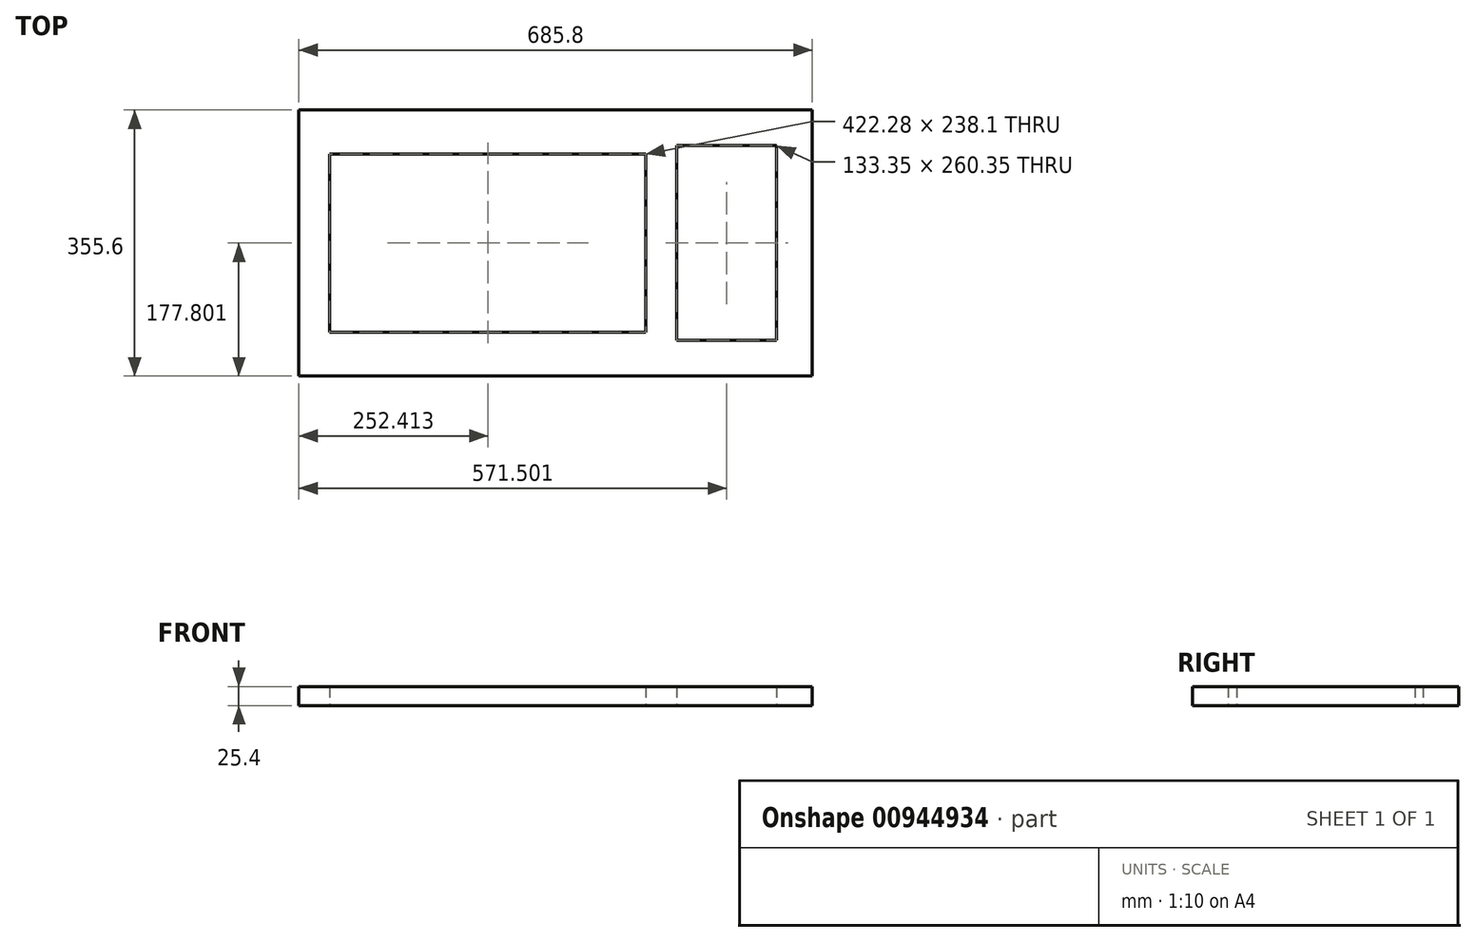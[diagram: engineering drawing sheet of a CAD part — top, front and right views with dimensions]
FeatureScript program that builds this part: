
annotation { "Feature Type Name" : "Feature", "Feature Type Description" : "" }
export const myFeature = defineFeature(function(context is Context, id is Id, definition is map)
    precondition{}
    {
        {
            var Q0;
            Q0=qCreatedBy(makeId("Top.planeOp"),FACE);
            var sketch = newSketch(context, id + "F0", { "sketchPlane" : qUnion([Q0])});
            skLineSegment(sketch, "E0.bottom", {"start": v(-348.34, 190.06) * mm, "end": v(337.46, 190.06) * mm});
            skLineSegment(sketch, "E0.top", {"start": v(-348.34, -165.54) * mm, "end": v(337.46, -165.54) * mm});
            skLineSegment(sketch, "E0.left", {"start": v(-348.34, 190.06) * mm, "end": v(-348.34, -165.54) * mm});
            skLineSegment(sketch, "E0.right", {"start": v(337.46, 190.06) * mm, "end": v(337.46, -165.54) * mm});
            skLineSegment(sketch, "E1.bottom", {"start": v(156.49, 142.44) * mm, "end": v(289.84, 142.44) * mm});
            skLineSegment(sketch, "E1.top", {"start": v(156.49, -117.91) * mm, "end": v(289.84, -117.91) * mm});
            skLineSegment(sketch, "E1.left", {"start": v(156.49, 142.44) * mm, "end": v(156.49, -117.91) * mm});
            skLineSegment(sketch, "E1.right", {"start": v(289.84, 142.44) * mm, "end": v(289.84, -117.91) * mm});
            skLineSegment(sketch, "E2.bottom", {"start": v(-307.06, 131.31) * mm, "end": v(115.21, 131.31) * mm});
            skLineSegment(sketch, "E2.top", {"start": v(-307.06, -106.79) * mm, "end": v(115.21, -106.79) * mm});
            skLineSegment(sketch, "E2.left", {"start": v(-307.06, 131.31) * mm, "end": v(-307.06, -106.79) * mm});
            skLineSegment(sketch, "E2.right", {"start": v(115.21, 131.31) * mm, "end": v(115.21, -106.79) * mm});
            skSolve(sketch);
        }
        {
            var Q0;
            Q0=makeQuery(id+"F0.imprint","IMPRINT",FACE,{"disambiguationData":[TD([[makeQuery(id+"F0.imprint","IMPRINT",EDGE,{"derivedFrom":sQuery(id+"F0.wireOp",EDGE,"E0.bottom")}),-1.0]])]});
            extrude(context, id + "F1", {"entities" : qUnion([Q0]), "depth" : 25.4 * mm, "offsetDistance" : 25.4 * mm});
        }
    });
